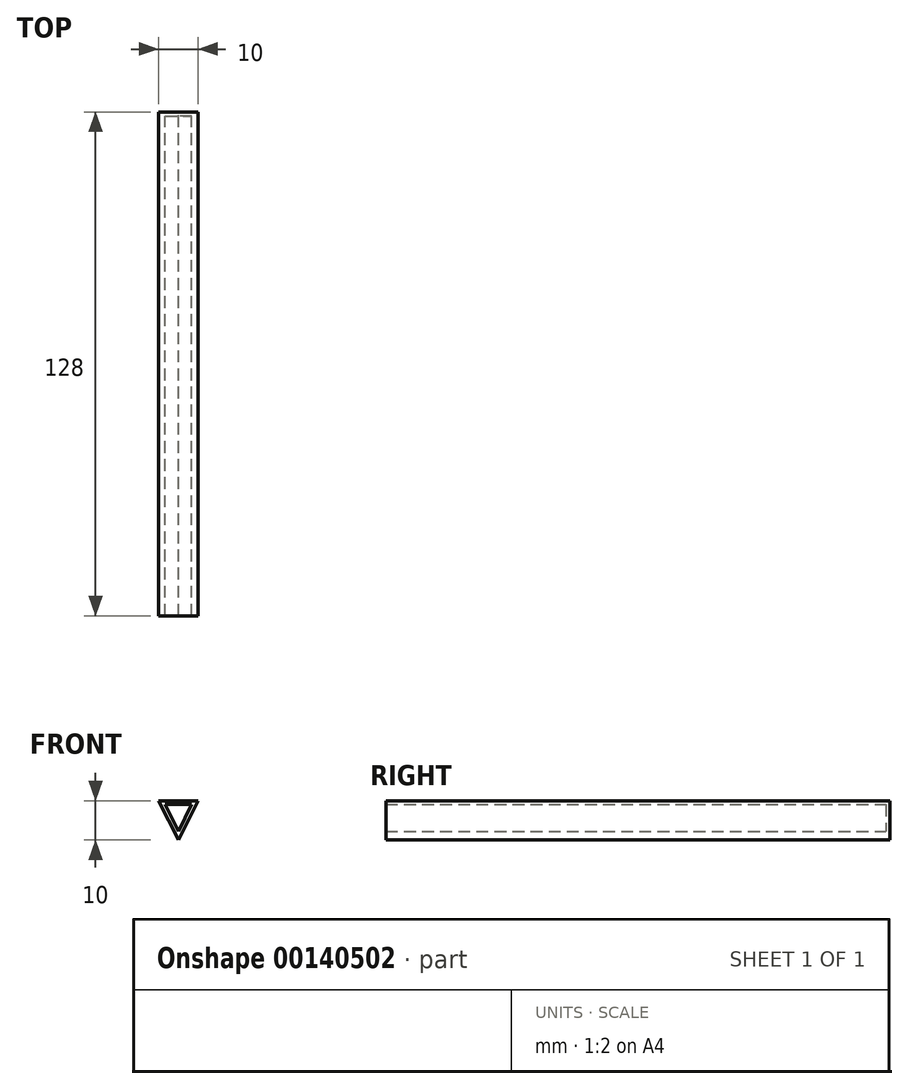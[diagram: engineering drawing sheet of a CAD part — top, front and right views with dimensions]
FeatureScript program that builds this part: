
annotation { "Feature Type Name" : "Feature", "Feature Type Description" : "" }
export const myFeature = defineFeature(function(context is Context, id is Id, definition is map)
    precondition{}
    {
        {
            var Q0;
            Q0=qCreatedBy(makeId("Front.planeOp"),FACE);
            var sketch = newSketch(context, id + "F0", { "sketchPlane" : qUnion([Q0])});
            skLineSegment(sketch, "E0", {"start": v(0, 0) * mm, "end": v(5, 0) * mm});
            skLineSegment(sketch, "E1", {"start": v(5, 0) * mm, "end": v(10, 0) * mm});
            skLineSegment(sketch, "E2", {"start": v(10, 0) * mm, "end": v(5, -10) * mm});
            skLineSegment(sketch, "E3", {"start": v(0, 0) * mm, "end": v(5, -10) * mm});
            skLineSegment(sketch, "E4.0", {"start": v(1.62, -1) * mm, "end": v(5, -1) * mm});
            skLineSegment(sketch, "E4.1", {"start": v(1.62, -1) * mm, "end": v(5, -7.76) * mm});
            skLineSegment(sketch, "E4.2", {"start": v(8.38, -1) * mm, "end": v(5, -7.76) * mm});
            skLineSegment(sketch, "E4.3", {"start": v(5, -1) * mm, "end": v(8.38, -1) * mm});
            skSolve(sketch);
        }
        {
            var Q0;
            Q0=makeQuery(id+"F0.imprint","IMPRINT",FACE,{"disambiguationData":[TD([[makeQuery(id+"F0.imprint","IMPRINT",EDGE,{"derivedFrom":sQuery(id+"F0.wireOp",EDGE,"E4.0")}),-1.0]])]});
            extrude(context, id + "F1", {"entities" : qUnion([Q0]), "depth" : 1 * mm});
        }
        {
            var Q0;
            Q0=makeQuery(id+"F0.imprint","IMPRINT",FACE,{"disambiguationData":[TD([[makeQuery(id+"F0.imprint","IMPRINT",EDGE,{"derivedFrom":sQuery(id+"F0.wireOp",EDGE,"E0")}),-1.0]])]});
            extrude(context, id + "F2", {"entities" : qUnion([Q0]), "operationType" : NewBodyOperationType.ADD, "depth" : 128 * mm});
        }
    });
